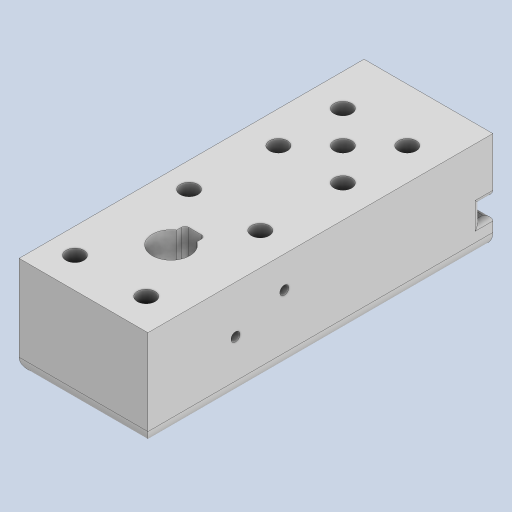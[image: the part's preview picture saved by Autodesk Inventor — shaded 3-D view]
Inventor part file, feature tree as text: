
AUTODESK INVENTOR PART (.ipt)
format: ipt  version: 2024 (Build 280153000, 153)  size: 548,352 bytes
history: native  units: mm
features: projected_geometry x17, extrude x16, sketch x16, fillet x2, plane x1
ambient origin geometry x8: Origin, YZ Plane, XZ Plane, XY Plane, X Axis, Y Axis, Z Axis, Center Point
bodies: Solid1 (feature_tree)
feature tree (52):
  extrude  "Extrusion1"  Depth=30.4mm
  extrude  "Extrusion2"  Depth=17.375mm
  extrude  "Extrusion3"  Depth=50.8mm
  extrude  "Extrusion4"  Depth=75.0mm TaperAngle=0.0deg
  extrude  "Extrusion5"  Depth=3.0mm
  extrude  "Extrusion6"  Depth=20.0mm TaperAngle=0.0deg
  extrude  "Extrusion7"  Depth=18.5mm
  extrude  "Extrusion8"  TaperAngle=0.0deg  [1 undecoded]
  extrude  "Extrusion9"  TaperAngle=0.0deg  [1 undecoded]
  extrude  "Extrusion10"  Depth=3.5mm
  plane  "Work Plane2"
  extrude  "Extrusion12"  TaperAngle=0.0deg  [1 undecoded]
  extrude  "Extrusion13"  Depth=3.5mm
  extrude  "Extrusion14"  TaperAngle=0.0deg  [1 undecoded]
  extrude  "Extrusion11"  Depth=2.5mm
  fillet  "Fillet1"  Radius=2.5mm
  fillet  "Fillet2"  Radius=3.0mm
  extrude  "Extrusion15"  Depth=3.0mm
  extrude  "Extrusion16"  Depth=3.5mm
  sketch  "Sketch1"  dims[d0=14.75mm d2=30.4mm]
  sketch  "Sketch5"  dims[d3=0.0mm d4=17.375mm]
  projected_geometry  "Projected Loop3"
  sketch  "Sketch6"  dims[d5=13.607143mm d6=50.8mm]
  projected_geometry  "Projected Loop4"
  sketch  "Sketch7"  dims[d7=12.375mm d8=75.0mm d9=0.0mm]
  projected_geometry  "Projected Loop5"
  sketch  "Sketch8"  dims[d16=8.5mm d17=3.0mm]
  projected_geometry  "Projected Loop6"
  sketch  "Sketch9"  dims[d18=16.5mm d19=0.0mm d20=20.0mm d21=0.0mm]
  projected_geometry  "Projected Loop7"
  sketch  "Sketch10"  dims[d22=20.0mm d23=18.5mm]
  projected_geometry  "Projected Loop8"
  projected_geometry  "Projected Loop9"
  sketch  "Sketch11"  dims[d24=0.0mm d25=0.0mm]
  projected_geometry  "Projected Loop10"
  sketch  "Sketch12"  dims[d26=0.0mm d27=0.0mm]
  projected_geometry  "Projected Loop11"
  sketch  "Sketch13"  dims[d28=3.5mm d29=14.75mm]
  projected_geometry  "Projected Loop12"
  sketch  "Sketch14"  dims[d30=1.0mm d31=0.0mm d32=0.0mm d33=0.0mm]
  projected_geometry  "Projected Loop13"
  sketch  "Sketch15"  dims[d34=26.125mm d35=0.0mm d37=3.5mm]
  projected_geometry  "Projected Loop14"
  sketch  "Sketch16"  dims[d38=18.662mm d39=0.0mm d40=0.0mm]
  projected_geometry  "Projected Loop15"
  sketch  "Sketch17"  dims[d41=0.0mm d42=0.0mm d43=2.5mm d44=2.5mm d45=3.0mm]
  projected_geometry  "Projected Loop16"
  sketch  "Sketch18"  dims[d46=6.5mm d47=3.0mm]
  sketch  "Sketch19"  dims[d48=3.0mm d49=3.0mm d50=3.0mm d51=3.0mm d52=2.0mm d53=2.0mm d54=0.0mm d55=0.0mm d56=0.0mm d57=0.0mm d58=10.0mm d59=20.0mm d60=25.0mm d61=0.0mm d62=0.0mm d63=12.7mm d64=12.7mm d65=12.7mm d66=12.7mm d67=13.607mm d68=13.607mm d69=13.607mm d70=9.0mm d71=0.0mm d72=13.607mm d73=13.607mm d74=0.0mm d75=0.0mm d76=0.0mm d77=50.8mm d79=25.4mm d80=25.4mm d81=25.4mm d82=0.0mm d83=0.0mm d84=25.4mm d85=25.4mm d86=13.607mm d87=13.607mm d88=13.607mm d89=13.607mm d90=0.0mm d91=9.0mm d92=6.5mm d93=0.0mm d94=0.0mm d95=5.0mm d96=0.0mm d97=2.0mm d98=10.0mm d99=34.513mm d100=25.4mm d101=39.775mm d102=0.0mm d103=42.775mm d104=12.7mm d105=0.0mm d106=13.607mm d107=18.0mm d108=6.0mm d109=12.7mm d110=50.8mm d111=25.4mm d113=0.0mm d115=25.4mm d116=25.4mm d117=25.4mm d118=0.0mm d119=12.7mm d120=12.7mm d122=67.5mm d123=33.75mm d124=45.0mm d125=45.0mm d126=0.0mm d127=0.0mm d128=10.0mm d129=22.5mm d130=12.7mm d131=22.5mm d132=7.0mm d133=7.0mm d134=7.0mm d135=7.0mm d136=7.0mm d137=7.0mm d138=7.0mm d139=7.0mm d140=7.0mm d141=34.513mm d142=34.0mm d143=25.0mm d144=0.0mm d145=3.5mm d146=82.25mm d147=12.375mm d148=0.0mm d149=0.0mm]
  projected_geometry  "Projected Loop17"
  projected_geometry  "Projected Loop18"
  projected_geometry  "Projected Loop19"
note: 4 required parameter values undecoded (feature->parameter linkage not recoverable at this tier; creation-order binding heuristic only, values carry confidence <= 0.55)
